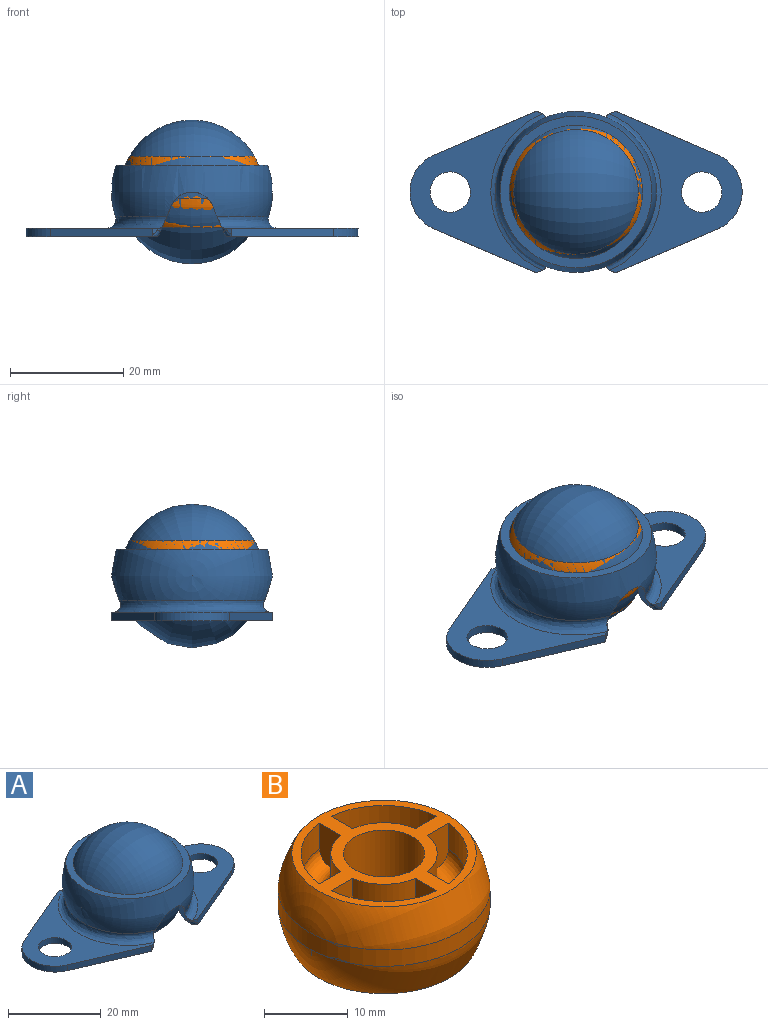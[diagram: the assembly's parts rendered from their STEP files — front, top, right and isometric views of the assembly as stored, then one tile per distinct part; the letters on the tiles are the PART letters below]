
ASSEMBLY  parts=2 mates=1
PART A: 41 faces, bbox 113.7x83.7x83.4 mm
  f0: cylinder r=3.57mm len=7.14mm, axis (0,0,1), area 34.2mm2, adj f10,f12
  f1: cylinder r=7.14mm len=13.12mm, axis (0,0,-1), area 25.4mm2, adj f2,f3,f10,f12
  f2: plane 18.08x7.75mm, normal (-0.39,-0.92,0), area 29.9mm2, adj f1,f10,f12,f15,f16
  f3: plane 18.08x7.76mm, normal (-0.39,0.92,0), area 29.9mm2, adj f1,f9,f10,f12,f13
  f4: cylinder r=3.57mm len=7.14mm, axis (0,0,1), area 34.2mm2, adj f19,f23
  f5: plane 18.08x7.75mm, normal (0.39,0.92,0), area 29.9mm2, adj f6,f8,f18,f19,f23
  f6: cylinder r=7.14mm len=13.12mm, axis (0,0,-1), area 25.4mm2, adj f5,f7,f19,f23
  f7: plane 18.08x7.76mm, normal (0.39,-0.92,0), area 29.9mm2, adj f6,f19,f21,f22,f23
  f8: plane 1.09x0.94mm, normal (-0.37,0.93,0), area 0.7mm2, adj f5,f18,f23,f24
  f9: plane 1.09x0.94mm, normal (0.37,0.93,0), area 0.7mm2, adj f3,f10,f13,f25
  f10: plane 28.58x23.45mm, normal (0,0,1), area 224.7mm2, adj f0,f1,f2,f3,f9,f15,f25,f27
  f11: cylinder r=2.54mm len=1.59mm, axis (0,-1,0), area 0.7mm2, adj f16,f26,f35
  f12: plane 28.69x23.25mm, normal (0,0,-1), area 227.2mm2, adj f0,f1,f2,f3,f13,f16,f26
  f13: bspline ~1.86x1.72mm, area 1.8mm2, adj f3,f9,f12,f14,f25,f26
  f14: cylinder r=2.54mm len=1.59mm, axis (0,-1,0), area 0.7mm2, adj f13,f26,f32
  f15: plane 1.09x0.94mm, normal (0.37,-0.93,0), area 0.7mm2, adj f2,f10,f16,f27
  f16: bspline ~1.86x1.72mm, area 1.8mm2, adj f2,f11,f12,f15,f26,f27
  f17: cylinder r=2.54mm len=1.59mm, axis (0,-1,0), area 0.7mm2, adj f18,f28,f30
  f18: bspline ~1.86x1.72mm, area 1.8mm2, adj f5,f8,f17,f19,f24,f28
  f19: plane 28.69x23.25mm, normal (0,0,-1), area 227.2mm2, adj f4,f5,f6,f7,f18,f21,f28
  f20: cylinder r=2.54mm len=1.59mm, axis (0,-1,0), area 0.7mm2, adj f21,f28,f37
  f21: bspline ~1.86x1.72mm, area 1.8mm2, adj f7,f19,f20,f22,f28,f29
  f22: plane 1.09x0.94mm, normal (-0.37,-0.93,0), area 0.7mm2, adj f7,f21,f23,f29
  f23: plane 28.58x23.45mm, normal (0,0,1), area 224.8mm2, adj f4,f5,f6,f7,f8,f22,f24,f29
  f24: cylinder r=1.02mm len=1.75mm, axis (0.38,0.15,-0.91), area 0.9mm2, adj f8,f18,f23,f30,f38
  f25: cylinder r=1.02mm len=1.75mm, axis (0.38,-0.15,0.91), area 0.9mm2, adj f9,f10,f13,f32,f34
  f26: revolved ~27.99x10.73mm, area 168.5mm2, adj f11,f12,f13,f14,f16,f32,f33,f35
  f27: cylinder r=1.02mm len=1.75mm, axis (-0.38,-0.15,-0.91), area 0.9mm2, adj f10,f15,f16,f34,f35
  f28: revolved ~27.99x10.73mm, area 168.5mm2, adj f17,f18,f19,f20,f21,f30,f33,f37
  f29: cylinder r=1.02mm len=1.75mm, axis (-0.38,0.15,0.91), area 0.9mm2, adj f21,f22,f23,f37,f38
  f30: plane 59.6x57.59mm, normal (-0.92,0,-0.39), area 8.5mm2, adj f17,f24,f28,f31,f33,f38,f40
  f31: cylinder r=3.97mm len=7.33mm, axis (0,-1,0), area 15mm2, adj f30,f32,f33,f40
  f32: plane 4.76x2.74mm, normal (0.92,0,-0.39), area 8.5mm2, adj f14,f25,f26,f31,f33,f34,f40
  f33: revolved ~25.38x25.38mm, area -674.4mm2, adj f26,f28,f30,f31,f32,f35,f36,f37
  f34: revolved ~28.44x10.63mm, area 99.8mm2, adj f10,f25,f27,f32,f35,f40
  f35: plane 4.76x2.74mm, normal (0.92,0,-0.39), area 8.5mm2, adj f11,f26,f27,f33,f34,f36,f40
  f36: cylinder r=3.97mm len=7.33mm, axis (0,-1,0), area 15mm2, adj f33,f35,f37,f40
  f37: plane 4.76x2.74mm, normal (-0.92,0,-0.39), area 8.5mm2, adj f20,f28,f29,f33,f36,f38,f40
  f38: revolved ~28.44x10.63mm, area 99.8mm2, adj f23,f24,f29,f30,f37,f40
  f39: plane 26.81x26.81mm, normal (0,0,1), area 128.9mm2, adj f33,f40
  f40: revolved ~28.42x28.42mm, area -860.6mm2, adj f30,f31,f32,f34,f35,f36,f37,f38
PART B: 47 faces, bbox 25.5x25.5x25.6 mm
  f0: revolved ~9.24x9.24mm, area 60.2mm2, adj f4,f5,f6,f7
  f1: revolved ~9.24x9.24mm, area 60.2mm2, adj f8,f9,f10,f11
  f2: revolved ~9.24x9.24mm, area 60.2mm2, adj f12,f13,f14,f15
  f3: revolved ~9.24x9.24mm, area 60.2mm2, adj f16,f17,f18,f19
  f4: cylinder r=9.92mm len=8.88mm, axis (0,0,1), area 51.4mm2, adj f0,f5,f7,f24
  f5: plane 5.73x3.76mm, normal (0,-1,0), area 18.6mm2, adj f0,f4,f6,f24
  f6: cylinder r=6.35mm len=5.28mm, axis (0,0,1), area 30.2mm2, adj f0,f5,f7,f24
  f7: plane 5.73x3.76mm, normal (-1,0,0), area 18.6mm2, adj f0,f4,f6,f24
  f8: cylinder r=9.92mm len=8.88mm, axis (0,0,1), area 51.4mm2, adj f1,f9,f11,f24
  f9: plane 5.73x3.76mm, normal (1,0,0), area 18.6mm2, adj f1,f8,f10,f24
  f10: cylinder r=6.35mm len=5.28mm, axis (0,0,1), area 30.2mm2, adj f1,f9,f11,f24
  f11: plane 5.73x3.76mm, normal (0,-1,0), area 18.6mm2, adj f1,f8,f10,f24
  f12: cylinder r=9.92mm len=8.88mm, axis (0,0,1), area 51.4mm2, adj f2,f13,f15,f24
  f13: plane 5.73x3.76mm, normal (0,1,0), area 18.6mm2, adj f2,f12,f14,f24
  f14: cylinder r=6.35mm len=5.28mm, axis (0,0,1), area 30.2mm2, adj f2,f13,f15,f24
  f15: plane 5.73x3.76mm, normal (1,0,0), area 18.6mm2, adj f2,f12,f14,f24
  f16: cylinder r=9.92mm len=8.88mm, axis (0,0,1), area 51.4mm2, adj f3,f17,f19,f24
  f17: plane 5.73x3.76mm, normal (-1,0,0), area 18.6mm2, adj f3,f16,f18,f24
  f18: cylinder r=6.35mm len=5.28mm, axis (0,0,1), area 30.2mm2, adj f3,f17,f19,f24
  f19: plane 5.73x3.76mm, normal (0,1,0), area 18.6mm2, adj f3,f16,f18,f24
  f20: revolved ~9.24x9.24mm, area 60.2mm2, adj f25,f26,f27,f28
  f21: revolved ~9.24x9.24mm, area 60.2mm2, adj f29,f30,f31,f32
  f22: revolved ~9.24x9.24mm, area 60.2mm2, adj f33,f34,f35,f36
  f23: revolved ~9.24x9.24mm, area 60.2mm2, adj f37,f38,f39,f40
  f24: plane 22x22mm, normal (0,0,1), area 152.3mm2, adj f4,f5,f6,f7,f8,f9,f10,f11
  f25: plane 5.73x3.76mm, normal (0,-1,0), area 18.6mm2, adj f20,f26,f28,f44
  f26: cylinder r=9.92mm len=8.88mm, axis (0,0,1), area 51.4mm2, adj f20,f25,f27,f44
  f27: plane 5.73x3.76mm, normal (-1,0,0), area 18.6mm2, adj f20,f26,f28,f44
  f28: cylinder r=6.35mm len=5.28mm, axis (0,0,1), area 30.2mm2, adj f20,f25,f27,f44
  f29: plane 5.73x3.76mm, normal (1,0,0), area 18.6mm2, adj f21,f30,f32,f44
  f30: cylinder r=9.92mm len=8.88mm, axis (0,0,1), area 51.4mm2, adj f21,f29,f31,f44
  f31: plane 5.73x3.76mm, normal (0,-1,0), area 18.6mm2, adj f21,f30,f32,f44
  f32: cylinder r=6.35mm len=5.28mm, axis (0,0,1), area 30.2mm2, adj f21,f29,f31,f44
  f33: cylinder r=9.92mm len=8.88mm, axis (0,0,1), area 51.4mm2, adj f22,f34,f36,f44
  f34: plane 5.73x3.76mm, normal (0,1,0), area 18.6mm2, adj f22,f33,f35,f44
  f35: cylinder r=6.35mm len=5.28mm, axis (0,0,1), area 30.2mm2, adj f22,f34,f36,f44
  f36: plane 5.73x3.76mm, normal (-1,0,0), area 18.6mm2, adj f22,f33,f35,f44
  f37: cylinder r=6.35mm len=5.28mm, axis (0,0,1), area 30.2mm2, adj f23,f38,f40,f44
  f38: plane 5.73x3.76mm, normal (0,1,0), area 18.6mm2, adj f23,f37,f39,f44
  f39: cylinder r=9.92mm len=8.88mm, axis (0,0,1), area 51.4mm2, adj f23,f38,f40,f44
  f40: plane 5.73x3.76mm, normal (1,0,0), area 18.6mm2, adj f23,f37,f39,f44
  f41: cylinder r=4.85mm len=12.7mm, axis (0,0,1), area 386.6mm2, adj f24,f44
  f42: cylinder r=0.8mm len=7.49mm, axis (0,0,1), area 11.3mm2, adj f43,f45,f46
  f43: revolved ~25.33x25.33mm, area 408.4mm2, adj f24,f42,f45
  f44: plane 22x22mm, normal (0,0,-1), area 152.2mm2, adj f25,f26,f27,f28,f29,f30,f31,f32
  f45: cylinder r=12.64mm len=25.29mm, axis (0,0,1), area 186.2mm2, adj f42,f43,f46
  f46: revolved ~25.33x25.33mm, area 408.7mm2, adj f42,f44,f45
PLACE A at identity fixed
PLACE B rot(axis=(0,0,1),10.8deg) t=(0,0,0)mm
MATE revolute B.f41 <-> A.f26  axis (0,0,1) through (0,0,0)mm
